# Revit family: 3030412D_3030412DC_MAST 12.0M Ø89 PL240
name_source: partatom
category: Lighting Fixtures
units: mm (PartAtom-declared; Revit-internal decimal feet)

## family parameters
Always vertical = Yes
Cut with Voids When Loaded = No
Light Source = No
Maintain Annotation Orientation = No
OmniClass Number = 23.80.70.14.21
OmniClass Title = Street and Roadway Lighting
Part Type = Normal
Room Calculation Point = No
Round Connector Dimension = Use Diameter
Shared = No
Work Plane-Based = No

## types (1)
- Avtrappede master
    Area = 9,91 m²
    Art.nr = 3030412D/3030412DC
    Art.nr CombiCoat = 3030412DC
    Art.nr VZN = 3030412D
    Bunndiameter = Ø170
    CE-godkjent = Ja
    Category = Avtrappede master
    Center of Gravity = X: -0,002 mm Y: 0,871 mm Z: 4691,724 mm
    Default Elevation = 0 mm  [stored 0 ft]
    Density = 7809,86 kg/m³
    Description = MAST 12.0M Ø89 PL240
    Design Status = 1
    Designer = khk
    El nr = 3640106/3640118
    Filnamn-VO = Standard
    Filnavn = MAST 12.0M Ø89 PL240
    Fotplate C/C bolter = 240mm
    Fundament = 3520240C
    Lyspunkthoyde = 12m
    Manufacturer = Vik Ørsta AS
    Mass = 156,53 kg
    Model = 3030412D_3030412DC
    Part Number = L10205
    Requested Accuracy = Low
    Revision Number = -
    Size = 0,0,0
    Sti&Filnamn-VO = Standard
    Stock Number = 3010308D
    Title = MAST 12.0M Ø89 PL240
    Toppdiameter = Ø89
    Volume = 0,02 m³

note: [stored X ft] marks values corroborated as IEEE doubles in the binary element streams (Revit-internal decimal feet)

## geometry (parser evidence)
native form markers: Sweep x2
no freeform markers — native parametric forms only
